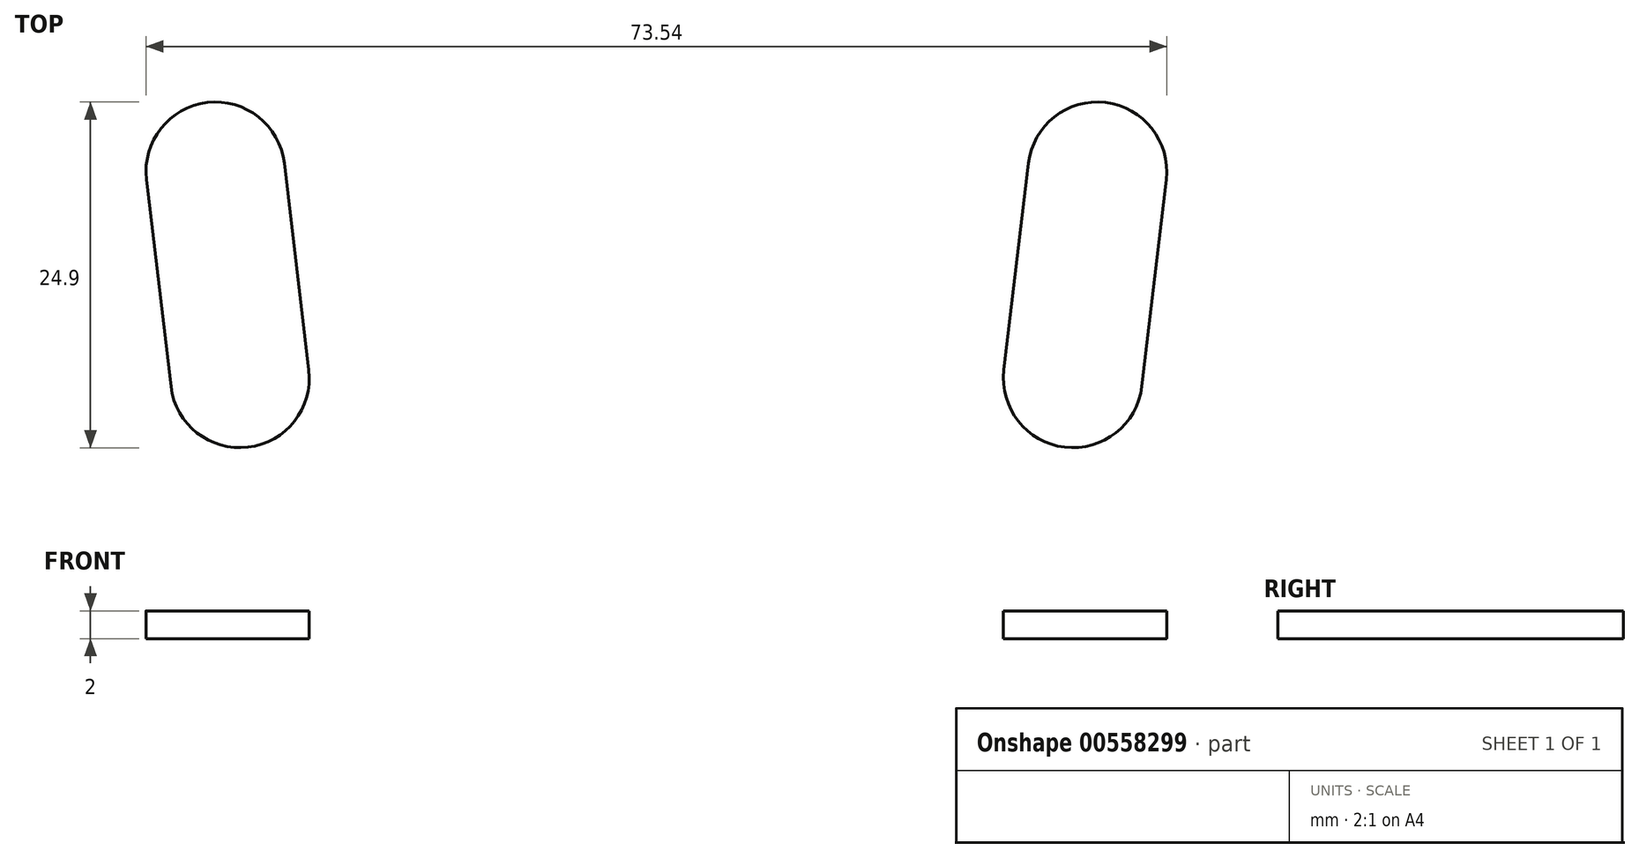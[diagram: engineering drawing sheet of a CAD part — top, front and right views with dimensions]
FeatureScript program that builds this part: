
annotation { "Feature Type Name" : "Feature", "Feature Type Description" : "" }
export const myFeature = defineFeature(function(context is Context, id is Id, definition is map)
    precondition{}
    {
        {
            var Q0;
            Q0=qCreatedBy(makeId("Top.planeOp"),FACE);
            var sketch = newSketch(context, id + "F0", { "sketchPlane" : qUnion([Q0])});
            skLineSegment(sketch, "E0", {"start": v(26.8, 33.78) * mm, "end": v(25.04, 18.89) * mm});
            skLineSegment(sketch, "E1", {"start": v(25.04, 18.89) * mm, "end": v(34.97, 17.71) * mm});
            skLineSegment(sketch, "E2", {"start": v(34.97, 17.71) * mm, "end": v(36.73, 32.6) * mm});
            skLineSegment(sketch, "E3", {"start": v(36.73, 32.6) * mm, "end": v(26.8, 33.78) * mm});
            skLineSegment(sketch, "E4", {"start": v(0, 0) * mm, "end": v(0, 71.2) * mm});
            skLineSegment(sketch, "E5.MirrorCS", {"start": v(-26.8, 33.78) * mm, "end": v(-25.04, 18.89) * mm});
            skLineSegment(sketch, "E6.MirrorCS", {"start": v(-36.73, 32.6) * mm, "end": v(-26.8, 33.78) * mm});
            skLineSegment(sketch, "E7.MirrorCS", {"start": v(-34.97, 17.71) * mm, "end": v(-36.73, 32.6) * mm});
            skLineSegment(sketch, "E8.MirrorCS", {"start": v(-25.04, 18.89) * mm, "end": v(-34.97, 17.71) * mm});
            skArc(sketch, "E9", {"start": v(36.73, 32.6) * mm, "mid": v(32.35, 38.16) * mm, "end": v(26.8, 33.78) * mm});
            skArc(sketch, "E10", {"start": v(25.04, 18.89) * mm, "mid": v(29.42, 13.34) * mm, "end": v(34.97, 17.71) * mm});
            skArc(sketch, "E11.MirrorCS", {"start": v(-25.04, 18.89) * mm, "mid": v(-29.42, 13.34) * mm, "end": v(-34.97, 17.71) * mm});
            skArc(sketch, "E12.MirrorCS", {"start": v(-36.73, 32.6) * mm, "mid": v(-32.35, 38.16) * mm, "end": v(-26.8, 33.78) * mm});
            skSolve(sketch);
        }
        {
            var Q0;
            Q0=makeQuery(id+"F0.imprint","IMPRINT",FACE,{"disambiguationData":[TD([[makeQuery(id+"F0.imprint","IMPRINT",EDGE,{"derivedFrom":sQuery(id+"F0.wireOp",EDGE,"E6.MirrorCS")}),1.0]])]});
            var Q1;
            Q1=makeQuery(id+"F0.imprint","IMPRINT",FACE,{"disambiguationData":[TD([[makeQuery(id+"F0.imprint","IMPRINT",EDGE,{"derivedFrom":sQuery(id+"F0.wireOp",EDGE,"E5.MirrorCS")}),-1.0]])]});
            var Q2;
            Q2=makeQuery(id+"F0.imprint","IMPRINT",FACE,{"disambiguationData":[TD([[makeQuery(id+"F0.imprint","IMPRINT",EDGE,{"derivedFrom":sQuery(id+"F0.wireOp",EDGE,"E8.MirrorCS")}),1.0]])]});
            var Q3;
            Q3=makeQuery(id+"F0.imprint","IMPRINT",FACE,{"disambiguationData":[TD([[makeQuery(id+"F0.imprint","IMPRINT",EDGE,{"derivedFrom":sQuery(id+"F0.wireOp",EDGE,"E1")}),-1.0]])]});
            var Q4;
            Q4=makeQuery(id+"F0.imprint","IMPRINT",FACE,{"disambiguationData":[TD([[makeQuery(id+"F0.imprint","IMPRINT",EDGE,{"derivedFrom":sQuery(id+"F0.wireOp",EDGE,"E0")}),1.0]])]});
            var Q5;
            Q5=makeQuery(id+"F0.imprint","IMPRINT",FACE,{"disambiguationData":[TD([[makeQuery(id+"F0.imprint","IMPRINT",EDGE,{"derivedFrom":sQuery(id+"F0.wireOp",EDGE,"E3")}),-1.0]])]});
            extrude(context, id + "F1", {"entities" : qUnion([Q0, Q1, Q2, Q3, Q4, Q5]), "depth" : 2 * mm, "offsetDistance" : 25.4 * mm});
        }
        {
            var Q0;
            Q0=qCreatedBy(makeId("Top.planeOp"),FACE);
            var sketch = newSketch(context, id + "F2", { "sketchPlane" : qUnion([Q0])});
            skLineSegment(sketch, "E13", {"start": v(25.04, 18.89) * mm, "end": v(-25.04, 18.89) * mm});
            skLineSegment(sketch, "E14", {"start": v(0, 18.89) * mm, "end": v(0, -26.01) * mm});
            skPoint(sketch, "E15", {"position": v(29.42, 13.34) * mm});
            skPoint(sketch, "E16", {"position": v(-30, 18.3) * mm});
            skLineSegment(sketch, "E17", {"start": v(-25.04, 18.89) * mm, "end": v(-34.97, 17.71) * mm});
            skLineSegment(sketch, "E18", {"start": v(25.04, 18.89) * mm, "end": v(34.97, 17.71) * mm});
            skPoint(sketch, "E19", {"position": v(30, 18.3) * mm});
            skFitSpline(sketch, "E20", {"points": [v(-30, 18.3) * mm, v(0, -26.01) * mm], "startDerivative": vector(4.15, -44.68) * mm, "endDerivative": vector(65.29, -5.1) * mm});
            skFitSpline(sketch, "E21.MirrorCS", {"points": [v(30, 18.3) * mm, v(0, -26.01) * mm], "startDerivative": vector(-4.15, -44.68) * mm, "endDerivative": vector(-65.29, -5.1) * mm});
            skSolve(sketch);
        }
        {
            var Q0;
            Q0=sQuery(id+"F2.wireOp",EDGE,"E20");
            var Q1;
            Q1=sQuery(id+"F2.wireOp",EDGE,"E21.MirrorCS");
            extrude(context, id + "F3", {"bodyType" : ToolBodyType.SURFACE, "surfaceEntities" : qUnion([Q0, Q1]), "oppositeDirection" : true, "depth" : 12 * mm, "offsetDistance" : 25.4 * mm});
        }
    });
